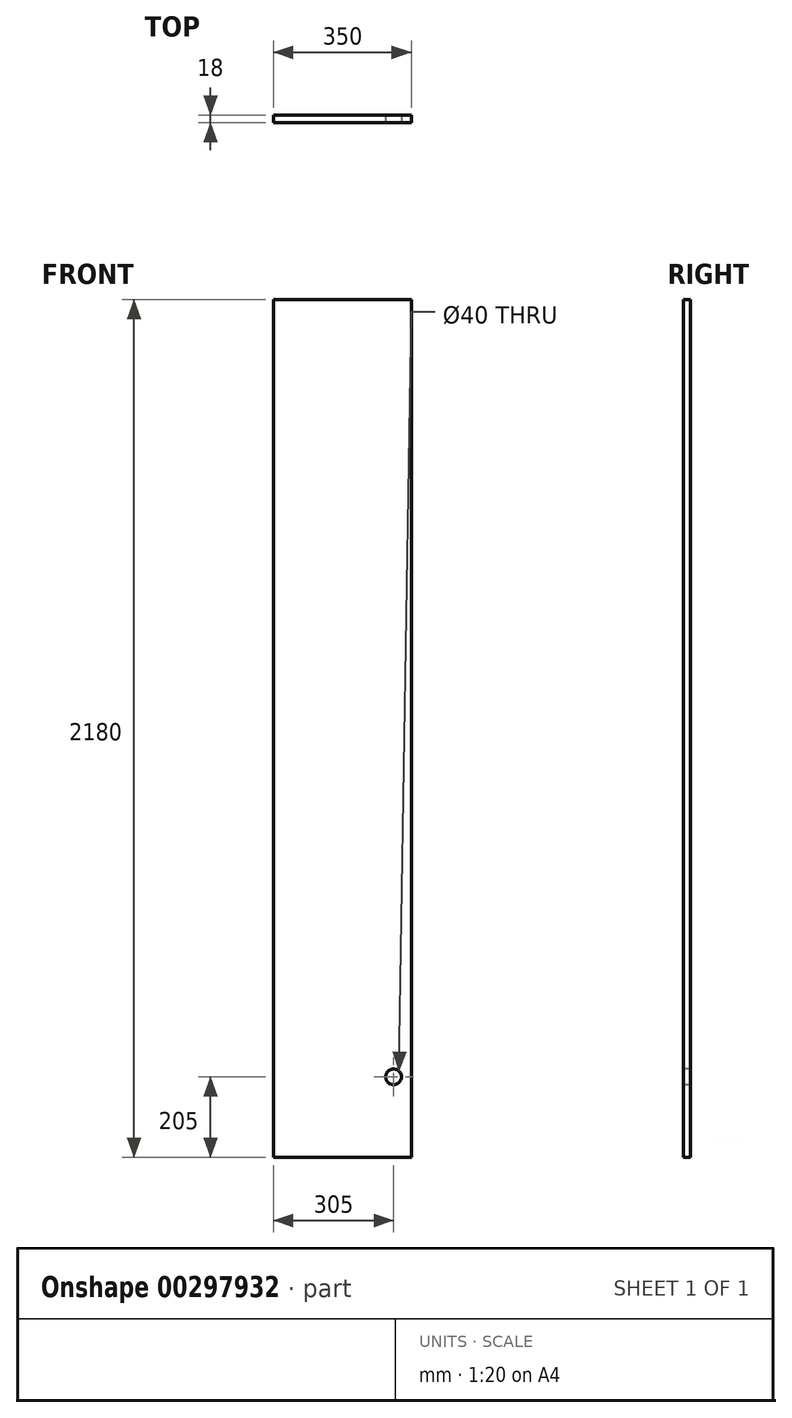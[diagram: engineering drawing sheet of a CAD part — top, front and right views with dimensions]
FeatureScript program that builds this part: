
annotation { "Feature Type Name" : "Feature", "Feature Type Description" : "" }
export const myFeature = defineFeature(function(context is Context, id is Id, definition is map)
    precondition{}
    {
        {
            var Q0;
            Q0=qCreatedBy(makeId("Front.planeOp"),FACE);
            var sketch = newSketch(context, id + "F0", { "sketchPlane" : qUnion([Q0])});
            skLineSegment(sketch, "E0.bottom", {"start": v(-175, 1090) * mm, "end": v(175, 1090) * mm});
            skLineSegment(sketch, "E0.top", {"start": v(-175, -1090) * mm, "end": v(175, -1090) * mm});
            skLineSegment(sketch, "E0.left", {"start": v(-175, 1090) * mm, "end": v(-175, -1090) * mm});
            skLineSegment(sketch, "E0.right", {"start": v(175, 1090) * mm, "end": v(175, -1090) * mm});
            skPoint(sketch, "E0.middle", {"position": v(0, 0) * mm});
            skSolve(sketch);
        }
        {
            var Q0;
            Q0=makeQuery(id+"F0.imprint","IMPRINT",FACE,{"disambiguationData":[TD([[makeQuery(id+"F0.imprint","IMPRINT",EDGE,{"derivedFrom":sQuery(id+"F0.wireOp",EDGE,"E0.bottom")}),-1.0]])]});
            extrude(context, id + "F1", {"entities" : qUnion([Q0]), "endBound" : BoundingType.SYMMETRIC, "depth" : 18 * mm});
        }
        {
            var Q0;
            Q0=makeQuery(id+"F1.opExtrude","CAP_FACE",FACE,{"disambiguationData":[OSD([sQuery(id+"F0.wireOp",EDGE,"E0.bottom"),sQuery(id+"F0.wireOp",EDGE,"E0.top"),sQuery(id+"F0.wireOp",EDGE,"E0.left"),sQuery(id+"F0.wireOp",EDGE,"E0.right")])],"isStart":false});
            var sketch = newSketch(context, id + "F2", { "sketchPlane" : qUnion([Q0])});
            skCircle(sketch, "E1", {"center": v(130, -885) * mm, "radius": 20 * mm});
            skLineSegment(sketch, "E2", {"start": v(130, -885) * mm, "end": v(229.57, -885) * mm});
            skSolve(sketch);
        }
        {
            var Q0;
            Q0=makeQuery(id+"F2.imprint","IMPRINT",FACE,{"disambiguationData":[TD([[makeQuery(id+"F2.imprint","IMPRINT",EDGE,{"derivedFrom":sQuery(id+"F2.wireOp",EDGE,"E1")}),1.0]])]});
            extrude(context, id + "F3", {"entities" : qUnion([Q0]), "operationType" : NewBodyOperationType.REMOVE, "oppositeDirection" : true, "depth" : 25 * mm});
        }
    });
